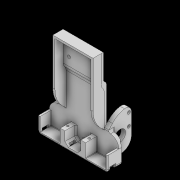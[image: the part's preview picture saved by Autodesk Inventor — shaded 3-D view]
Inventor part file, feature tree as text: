
AUTODESK INVENTOR PART (.ipt)
format: ipt  version: 2021 (Build 250183000, 183)  size: 603,136 bytes
history: native  units: mm
features: reference x30, fillet x17, extrude x15, sketch x15, other x8, direct_edit x5, move_body x5, plane x2, projected_geometry x2, chamfer x1, mirror x1
ambient origin geometry x8: Origin, YZ Plane, XZ Plane, XY Plane, X Axis, Y Axis, Z Axis, Center Point
bodies: Solid1 (feature_tree)
feature tree (101):
  plane  "Work Plane1"
  extrude  "Extrusion1"  Depth=0.5mm
  fillet  "Fillet1"  Radius=0.5mm
  fillet  "Fillet2"  Radius=0.2mm
  fillet  "Fillet3"  Radius=0.5mm
  extrude  "Extrusion2"  Depth=5.0mm TaperAngle=0.0deg
  extrude  "Extrusion3"  Depth=1.0mm
  fillet  "Fillet4"  Radius=24.25mm
  fillet  "Fillet5"  Radius=2.5mm
  extrude  "Extrusion4"  Depth=7.0mm
  direct_edit  "Direct Edit1"
  extrude  "Extrusion6"  Depth=4.0mm
  chamfer  "Chamfer1"  Distance=12.0mm
  extrude  "Extrusion8"  Depth=0.5mm
  extrude  "Extrusion9"  Depth=13.0mm TaperAngle=0.0deg
  extrude  "Extrusion10"  Depth=1.0mm
  fillet  "Fillet6"  Radius=0.5mm
  fillet  "Fillet7"  Radius=2.0mm
  fillet  "Fillet8"  Radius=23.5mm
  fillet  "Fillet9"  Radius=0.5mm
  mirror  "Mirror2"
  direct_edit  "Direct Edit2"
  fillet  "Fillet10"  Radius=1.0mm
  extrude  "Extrusion11"  Depth=5.0mm TaperAngle=45.0deg
  extrude  "Extrusion12"  Depth=3.0mm
  fillet  "Fillet11"  Radius=21.25mm
  fillet  "Fillet12"  Radius=35.0mm
  direct_edit  "Direct Edit3"
  extrude  "Extrusion13"  Depth=1.0mm TaperAngle=0.0deg
  extrude  "Extrusion14"  Depth=0.5mm
  fillet  "Fillet13"  Radius=10.5mm
  fillet  "Fillet14"  Radius=2.5mm
  extrude  "Extrusion15"  Depth=1.0mm
  sketch  "Sketch16"  dims[d63=3.0mm d64=0.5mm d65=10.5mm d66=2.5mm]
  plane  "Work Plane2"
  extrude  "Extrusion16"  Depth=1.0mm TaperAngle=0.0deg
  fillet  "Fillet15"  Radius=2.0mm
  fillet  "Fillet16"  Radius=2.0mm
  extrude  "Extrusion17"  Depth=1.0mm
  direct_edit  "Direct Edit4"
  direct_edit  "Direct Edit5"
  fillet  "Fillet17"  Radius=2.5mm
  sketch  "Sketch1"  dims[d0=0.5mm d1=0.5mm d2=0.5mm d3=0.2mm d4=0.5mm]
  reference  "Reference1"
  reference  "Reference2"
  reference  "Reference3"
  reference  "Reference4"
  reference  "Reference5"
  reference  "Reference6"
  reference  "Reference7"
  reference  "Reference8"
  reference  "Reference9"
  reference  "Reference10"
  sketch  "Sketch2"  dims[d5=3.0mm d6=5.0mm d7=0.0mm]
  sketch  "Sketch3"  dims[d8=1.0mm d9=15.0mm d10=24.25mm d11=2.5mm]
  reference  "Reference11"
  reference  "Reference12"
  reference  "Reference13"
  reference  "Reference14"
  sketch  "Sketch4"  dims[d12=12.5mm d13=7.0mm]
  projected_geometry  "Projected Loop1"
  reference  "Reference15"
  reference  "Reference16"
  sketch  "Sketch6"  dims[d14=1.0mm d15=4.0mm]
  reference  "Reference19"
  reference  "Reference20"
  sketch  "Sketch8"  dims[d16=1.0mm d17=12.0mm d18=0.0mm]
  sketch  "Sketch9"  dims[d19=0.5mm d20=0.5mm]
  sketch  "Sketch10"  dims[d21=0.5mm d22=13.0mm d23=0.0mm]
  projected_geometry  "Projected Loop2"
  reference  "Reference21"
  sketch  "Sketch11"  dims[d24=1.0mm d25=2.0mm d27=0.5mm d28=2.0mm d29=23.5mm d30=0.0mm]
  reference  "Reference22"
  sketch  "Sketch12"  dims[d31=0.0mm d32=0.0mm d33=-2.0mm d37=0.5mm d38=1.0mm]
  reference  "Reference23"
  reference  "Reference24"
  sketch  "Sketch13"  dims[d39=21.25mm d40=0.0mm d48=5.0mm d49=2.0mm d50=45.0deg]
  reference  "Reference25"
  reference  "Reference26"
  reference  "Reference27"
  sketch  "Sketch14"  dims[d54=7.0mm d55=3.0mm d56=21.25mm d57=0.0mm d58=35.0mm]
  sketch  "Sketch15"  dims[d59=1.0mm d60=0.0mm d61=2.0mm d62=0.0mm]
  reference  "Reference28"
  reference  "Reference29"
  reference  "Reference30"
  reference  "Reference31"
  reference  "Reference32"
  sketch  "Sketch17"  dims[d67=3.0mm d68=3.0mm d69=0.0mm d70=0.0mm d71=1.0mm d72=2.0mm d73=2.0mm d74=0.0mm d75=0.5mm d76=2.5mm d77=2.5mm d78=10.0mm d79=0.0mm d80=2.75mm d81=0.5mm d82=0.0mm d83=0.0mm d84=49.5mm d85=0.5mm d86=5.0mm d87=2.497835mm d88=2.497835mm d89=10.0mm d90=0.0mm d91=0.0mm d92=0.0mm d93=6.75mm d94=2.75mm d95=0.5mm d96=0.5mm d97=10.0mm d98=0.0mm d99=2.5mm d100=2.5mm d101=2.0mm d102=10.0mm d103=0.0mm d104=30.25mm d105=1.75mm d106=2.5mm d107=10.0mm d108=0.0mm d109=0.0mm d110=0.0mm d111=-3.749mm d112=0.0mm d113=0.0mm d114=-1.002165mm d115=1.0mm]
  parser-record x1  (decoder bookkeeping rows leaked as tree rows — omitted from the tree; the rows remain in map.json)
  other  "cylinderAssemblyV4.iam"
  other  "Hydr_CylinV4:1"
  other  "SG90-servo-motor:1"
  other  "BodyV4_Right:1"
  other  "rotarynozzle:1"
  other  "endcap:1"
  move_body  "Move1"
  move_body  "Move2"
  other  "SG90-servo-motor_MIR_Left:1"
  move_body  "Move3"
  move_body  "Move4"
  move_body  "Move5"
note: 1 file-system path scrubbed to <path> (originals preserved in map.json)
